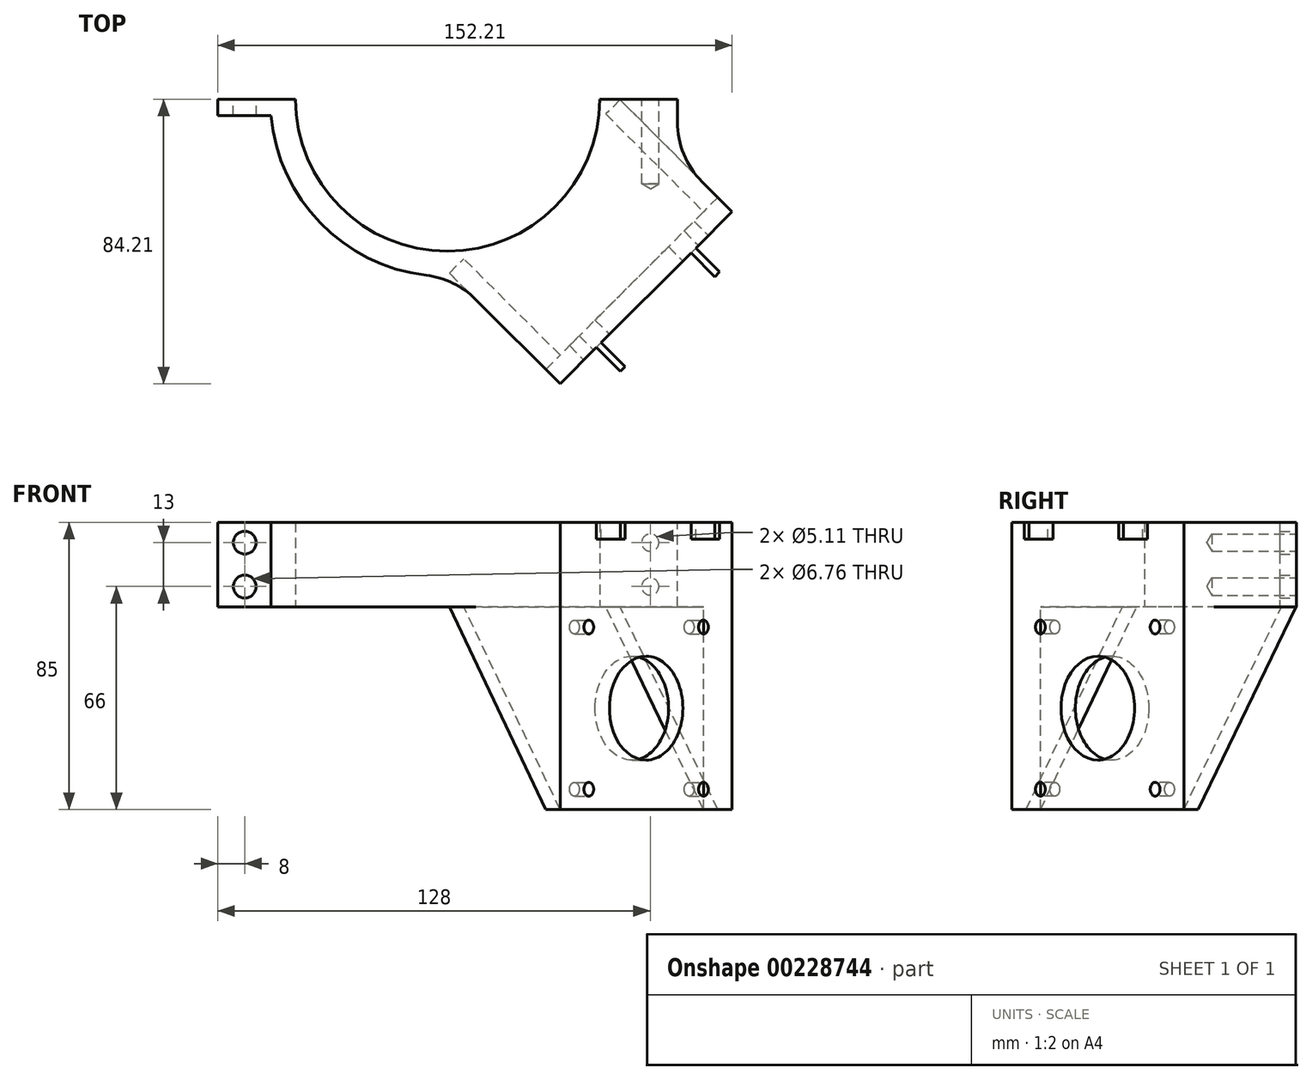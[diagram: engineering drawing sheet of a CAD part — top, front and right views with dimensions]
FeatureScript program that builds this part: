
annotation { "Feature Type Name" : "Feature", "Feature Type Description" : "" }
export const myFeature = defineFeature(function(context is Context, id is Id, definition is map)
    precondition{}
    {
        {
            var Q0;
            Q0=qCreatedBy(makeId("Top.planeOp"),FACE);
            var sketch = newSketch(context, id + "F0", { "sketchPlane" : qUnion([Q0])});
            skArc(sketch, "E0", {"start": v(-45, 0) * mm, "mid": v(0, -45) * mm, "end": v(45, 0) * mm});
            skArc(sketch, "E1", {"start": v(-52.27, -4.88) * mm, "mid": v(-31.78, -41.79) * mm, "end": v(9.25, -51.68) * mm});
            skLineSegment(sketch, "E2", {"start": v(-45, 0) * mm, "end": v(-68, 0) * mm});
            skLineSegment(sketch, "E3", {"start": v(-68, 0) * mm, "end": v(-68, -4.88) * mm});
            skLineSegment(sketch, "E4", {"start": v(-68, -4.88) * mm, "end": v(-52.27, -4.88) * mm});
            skLineSegment(sketch, "E5", {"start": v(45, 0) * mm, "end": v(68, 0) * mm});
            skLineSegment(sketch, "E6", {"start": v(68, 0) * mm, "end": v(68, -25.57) * mm});
            skPoint(sketch, "E7.orphan", {"position": v(52.5, 0) * mm});
            skLineSegment(sketch, "E8", {"start": v(0, 0) * mm, "end": v(69.96, -69.96) * mm, "construction": true});
            skLineSegment(sketch, "E9", {"start": v(68, -25.57) * mm, "end": v(79.96, -37.54) * mm});
            skLineSegment(sketch, "E10", {"start": v(79.96, -37.54) * mm, "end": v(37.54, -79.96) * mm});
            skLineSegment(sketch, "E11", {"start": v(37.54, -79.96) * mm, "end": v(9.25, -51.68) * mm});
            skPoint(sketch, "E12.orphan", {"position": v(68, -4.88) * mm});
            skSolve(sketch);
        }
        {
            var Q0;
            Q0 = qSketchRegion(id + "F0", true);
            extrude(context, id + "F1", {"entities" : qUnion([Q0]), "depth" : 25 * mm});
        }
        {
            var Q0;
            Q0=makeQuery(id+"F1.opExtrude","CAP_FACE",FACE,{"disambiguationData":[OSD([sQuery(id+"F0.wireOp",EDGE,"E0"),sQuery(id+"F0.wireOp",EDGE,"E1"),sQuery(id+"F0.wireOp",EDGE,"E2"),sQuery(id+"F0.wireOp",EDGE,"E3"),sQuery(id+"F0.wireOp",EDGE,"E4"),sQuery(id+"F0.wireOp",EDGE,"E5"),sQuery(id+"F0.wireOp",EDGE,"E6"),sQuery(id+"F0.wireOp",EDGE,"vUzMyOly-JOfE-7hCi-1u2C-14JDmTcw4MLE"),sQuery(id+"F0.wireOp",EDGE,"E9"),sQuery(id+"F0.wireOp",EDGE,"E10"),sQuery(id+"F0.wireOp",EDGE,"E11"),sQuery(id+"F0.wireOp",EDGE,"646cdaaa-5258-48e4-b4b1-44ca3091abd8.trimOffspring")])],"isStart":true});
            var sketch = newSketch(context, id + "F2", { "sketchPlane" : qUnion([Q0])});
            skLineSegment(sketch, "E13", {"start": v(37.54, 79.96) * mm, "end": v(79.96, 37.54) * mm});
            skLineSegment(sketch, "E14", {"start": v(79.96, 37.54) * mm, "end": v(75.72, 33.3) * mm});
            skLineSegment(sketch, "E15", {"start": v(75.72, 33.3) * mm, "end": v(33.3, 75.72) * mm});
            skLineSegment(sketch, "E16", {"start": v(33.3, 75.72) * mm, "end": v(37.54, 79.96) * mm});
            skSolve(sketch);
        }
        {
            var Q0;
            Q0 = qSketchRegion(id + "F2", true);
            extrude(context, id + "F3", {"entities" : qUnion([Q0]), "operationType" : NewBodyOperationType.ADD, "depth" : 60 * mm});
        }
        {
            var Q0;
            Q0=makeQuery(id+"F3.boolean.opBoolean","MERGE",FACE,{"derivedFrom":[makeQuery(id+"F1.opExtrude","SWEPT_FACE",FACE,{"disambiguationData":[OSD([sQuery(id+"F0.wireOp",EDGE,"E10")])]}),makeQuery(id+"F3.opExtrude","SWEPT_FACE",FACE,{"disambiguationData":[OSD([sQuery(id+"F2.wireOp",EDGE,"E13")])]})]});
            var sketch = newSketch(context, id + "F4", { "sketchPlane" : qUnion([Q0])});
            skCircle(sketch, "E17", {"center": v(0, -30) * mm, "radius": 15.37 * mm});
            skPoint(sketch, "E17.centerSnap0", {"position": v(0, -60) * mm});
            skLineSegment(sketch, "E18.direction1", {"start": v(-24, -54) * mm, "end": v(24, -54) * mm, "construction": true});
            skLineSegment(sketch, "E18.direction2", {"start": v(-24, -54) * mm, "end": v(-24, -6) * mm, "construction": true});
            skPoint(sketch, "E19", {"position": v(-24, -6) * mm});
            skPoint(sketch, "E20", {"position": v(-24, -54) * mm});
            skPoint(sketch, "E21", {"position": v(24, -54) * mm});
            skPoint(sketch, "E22", {"position": v(24, -6) * mm});
            skSolve(sketch);
        }
        {
            var Q0;
            Q0 = qSketchRegion(id + "F4", true);
            extrude(context, id + "F5", {"entities" : qUnion([Q0]), "operationType" : NewBodyOperationType.REMOVE, "endBound" : BoundingType.THROUGH_ALL, "oppositeDirection" : true, "depth" : 25 * mm});
        }
        {
            var Q0;
            Q0=makeQuery(id+"F1.opExtrude","CAP_FACE",FACE,{"disambiguationData":[OSD([sQuery(id+"F0.wireOp",EDGE,"E0"),sQuery(id+"F0.wireOp",EDGE,"E1"),sQuery(id+"F0.wireOp",EDGE,"E2"),sQuery(id+"F0.wireOp",EDGE,"E3"),sQuery(id+"F0.wireOp",EDGE,"E4"),sQuery(id+"F0.wireOp",EDGE,"E5"),sQuery(id+"F0.wireOp",EDGE,"E6"),sQuery(id+"F0.wireOp",EDGE,"vUzMyOly-JOfE-7hCi-1u2C-14JDmTcw4MLE"),sQuery(id+"F0.wireOp",EDGE,"E9"),sQuery(id+"F0.wireOp",EDGE,"E10"),sQuery(id+"F0.wireOp",EDGE,"E11"),sQuery(id+"F0.wireOp",EDGE,"646cdaaa-5258-48e4-b4b1-44ca3091abd8.trimOffspring")])],"isStart":false});
            var sketch = newSketch(context, id + "F6", { "sketchPlane" : qUnion([Q0])});
            skLineSegment(sketch, "E23", {"start": v(-68, 0) * mm, "end": v(79.96, 0) * mm, "construction": true});
            skSolve(sketch);
        }
        {
            var Q0;
            Q0=makeQuery(id+"F3.boolean.opBoolean","MERGE",FACE,{"derivedFrom":[makeQuery(id+"F1.opExtrude","SWEPT_FACE",FACE,{"disambiguationData":[OSD([sQuery(id+"F0.wireOp",EDGE,"E11")])]}),makeQuery(id+"F3.opExtrude","SWEPT_FACE",FACE,{"disambiguationData":[OSD([sQuery(id+"F2.wireOp",EDGE,"E16")])]})]});
            var sketch = newSketch(context, id + "F7", { "sketchPlane" : qUnion([Q0])});
            skLineSegment(sketch, "E24", {"start": v(83.08, 25) * mm, "end": v(83.08, -60) * mm});
            skLineSegment(sketch, "E25", {"start": v(83.08, -60) * mm, "end": v(77.08, -60) * mm});
            skLineSegment(sketch, "E26", {"start": v(77.08, -60) * mm, "end": v(36.79, 0) * mm});
            skLineSegment(sketch, "E27", {"start": v(36.79, 0) * mm, "end": v(36.79, 25) * mm});
            skLineSegment(sketch, "E28", {"start": v(36.79, 25) * mm, "end": v(83.08, 25) * mm});
            skSolve(sketch);
        }
        {
            var Q0;
            Q0 = qSketchRegion(id + "F7", true);
            extrude(context, id + "F8", {"entities" : qUnion([Q0]), "operationType" : NewBodyOperationType.ADD, "depth" : 6 * mm});
        }
        {
            var Q0;
            Q0=makeQuery(id+"F3.boolean.opBoolean","MERGE",FACE,{"derivedFrom":[makeQuery(id+"F1.opExtrude","SWEPT_FACE",FACE,{"disambiguationData":[OSD([sQuery(id+"F0.wireOp",EDGE,"E9")])]}),makeQuery(id+"F3.opExtrude","SWEPT_FACE",FACE,{"disambiguationData":[OSD([sQuery(id+"F2.wireOp",EDGE,"E14")])]})]});
            var sketch = newSketch(context, id + "F9", { "sketchPlane" : qUnion([Q0])});
            skLineSegment(sketch, "E29", {"start": v(-83.08, -60) * mm, "end": v(-83.08, 25) * mm});
            skLineSegment(sketch, "E30", {"start": v(-83.08, 25) * mm, "end": v(-36.18, 25) * mm});
            skLineSegment(sketch, "E31", {"start": v(-77.08, -60) * mm, "end": v(-83.08, -60) * mm});
            skLineSegment(sketch, "E32", {"start": v(-77.08, -60) * mm, "end": v(-36.18, 0) * mm});
            skLineSegment(sketch, "E33", {"start": v(-36.18, 0) * mm, "end": v(-36.18, 25) * mm});
            skSolve(sketch);
        }
        {
            var Q0;
            Q0 = qSketchRegion(id + "F9", true);
            extrude(context, id + "F10", {"entities" : qUnion([Q0]), "operationType" : NewBodyOperationType.ADD, "depth" : 6 * mm});
        }
        {
            var Q0;
            Q0=makeQuery(id+"F8.boolean.opBoolean","INTERSECT",EDGE,{"derivedFrom":[makeQuery(id+"F1.opExtrude","SWEPT_FACE",FACE,{"disambiguationData":[OSD([sQuery(id+"F0.wireOp",EDGE,"E1")])]}),makeQuery(id+"F8.opExtrude","CAP_FACE",FACE,{"disambiguationData":[OSD([sQuery(id+"F7.wireOp",EDGE,"E24"),sQuery(id+"F7.wireOp",EDGE,"E25"),sQuery(id+"F7.wireOp",EDGE,"E26"),sQuery(id+"F7.wireOp",EDGE,"E27"),sQuery(id+"F7.wireOp",EDGE,"E28")])],"isStart":false})]});
            fillet(context, id + "F11", {"entities" : qUnion([Q0]), "radius" : 25 * mm, "tangentPropagation" : true, "allowEdgeOverflow" : false});
        }
        {
            var Q0;
            Q0=makeQuery(id+"F10.boolean.opBoolean","INTERSECT",EDGE,{"derivedFrom":[makeQuery(id+"F1.opExtrude","SWEPT_FACE",FACE,{"disambiguationData":[OSD([sQuery(id+"F0.wireOp",EDGE,"E6")])]}),makeQuery(id+"F10.opExtrude","CAP_FACE",FACE,{"disambiguationData":[OSD([sQuery(id+"F9.wireOp",EDGE,"E29"),sQuery(id+"F9.wireOp",EDGE,"E30"),sQuery(id+"F9.wireOp",EDGE,"E31"),sQuery(id+"F9.wireOp",EDGE,"E32"),sQuery(id+"F9.wireOp",EDGE,"E33")])],"isStart":false})]});
            fillet(context, id + "F12", {"entities" : qUnion([Q0]), "radius" : 25 * mm, "tangentPropagation" : true, "allowEdgeOverflow" : false});
        }
        {
            var Q0;
            Q0=makeQuery(id+"F1.opExtrude","SWEPT_FACE",FACE,{"disambiguationData":[OSD([sQuery(id+"F0.wireOp",EDGE,"E2")])]});
            var sketch = newSketch(context, id + "F13", { "sketchPlane" : qUnion([Q0])});
            skLineSegment(sketch, "E34", {"start": v(60, -9.06) * mm, "end": v(60, 40.75) * mm, "construction": true});
            skLineSegment(sketch, "E35", {"start": v(-60, -8.44) * mm, "end": v(-60, 38.68) * mm, "construction": true});
            skPoint(sketch, "E36", {"position": v(60, 6) * mm});
            skPoint(sketch, "E37", {"position": v(60, 19) * mm});
            skPoint(sketch, "E38", {"position": v(-60, 6) * mm});
            skPoint(sketch, "E39", {"position": v(-60, 19) * mm});
            skSolve(sketch);
        }
        {
            var Q0;
            Q0=sQuery(id+"F13.wireOp",VERTEX,"E38");
            var Q1;
            Q1=sQuery(id+"F13.wireOp",VERTEX,"E39");
            var Q2;
            Q2=makeQuery(id+"F1.opExtrude","SWEPT_BODY",BODY,{"disambiguationData":[OSD([sQuery(id+"F0.wireOp",EDGE,"E0"),sQuery(id+"F0.wireOp",EDGE,"E1"),sQuery(id+"F0.wireOp",EDGE,"E2"),sQuery(id+"F0.wireOp",EDGE,"E3"),sQuery(id+"F0.wireOp",EDGE,"E4"),sQuery(id+"F0.wireOp",EDGE,"E5"),sQuery(id+"F0.wireOp",EDGE,"E6"),sQuery(id+"F0.wireOp",EDGE,"E9"),sQuery(id+"F0.wireOp",EDGE,"E10"),sQuery(id+"F0.wireOp",EDGE,"E11")])]});
            hole(context, id + "F14", {"style" : HoleStyle.SIMPLE, "endStyle" : HoleEndStyle.BLIND, "standardTappedOrClearance" : lookupTablePath({ "standard" : "ANSI", "engagement" : "75%", "pitch" : "20 tpi", "size" : "1/4", "type" : "Tapped" }), "standardBlindInLast" : lookupTablePath({ "standard" : "ANSI", "engagement" : "75%", "pitch" : "20 tpi", "size" : "1/4", "type" : "Tapped" }), "holeDiameter" : 5.1 * mm, "holeDepth" : 25 * mm, "locations" : qUnion([Q0, Q1]), "scope" : qUnion([Q2]), "majorDiameter" : 6.35 * mm});
        }
        {
            var Q0;
            Q0=sQuery(id+"F13.wireOp",VERTEX,"E36");
            var Q1;
            Q1=sQuery(id+"F13.wireOp",VERTEX,"E37");
            var Q2;
            Q2=makeQuery(id+"F1.opExtrude","SWEPT_BODY",BODY,{"disambiguationData":[OSD([sQuery(id+"F0.wireOp",EDGE,"E0"),sQuery(id+"F0.wireOp",EDGE,"E1"),sQuery(id+"F0.wireOp",EDGE,"E2"),sQuery(id+"F0.wireOp",EDGE,"E3"),sQuery(id+"F0.wireOp",EDGE,"E4"),sQuery(id+"F0.wireOp",EDGE,"E5"),sQuery(id+"F0.wireOp",EDGE,"E6"),sQuery(id+"F0.wireOp",EDGE,"E9"),sQuery(id+"F0.wireOp",EDGE,"E10"),sQuery(id+"F0.wireOp",EDGE,"E11")])]});
            hole(context, id + "F15", {"style" : HoleStyle.SIMPLE, "endStyle" : HoleEndStyle.BLIND, "standardTappedOrClearance" : lookupTablePath({ "standard" : "ANSI", "fit" : "Normal (ASME)", "size" : "1/4", "type" : "Clearance" }), "standardBlindInLast" : lookupTablePath({ "fit" : "Free", "standard" : "ANSI", "size" : "1/4", "type" : "Clearance" }), "holeDiameter" : 6.76 * mm, "holeDepth" : 25 * mm, "locations" : qUnion([Q0, Q1]), "scope" : qUnion([Q2])});
        }
        {
            var Q0;
            Q0=sQuery(id+"F4.wireOp",VERTEX,"E19");
            var Q1;
            Q1=sQuery(id+"F4.wireOp",VERTEX,"E22");
            var Q2;
            Q2=sQuery(id+"F4.wireOp",VERTEX,"E21");
            var Q3;
            Q3=sQuery(id+"F4.wireOp",VERTEX,"E20");
            var Q4;
            Q4=makeQuery(id+"F1.opExtrude","SWEPT_BODY",BODY,{"disambiguationData":[OSD([sQuery(id+"F0.wireOp",EDGE,"E0"),sQuery(id+"F0.wireOp",EDGE,"E1"),sQuery(id+"F0.wireOp",EDGE,"E2"),sQuery(id+"F0.wireOp",EDGE,"E3"),sQuery(id+"F0.wireOp",EDGE,"E4"),sQuery(id+"F0.wireOp",EDGE,"E5"),sQuery(id+"F0.wireOp",EDGE,"E6"),sQuery(id+"F0.wireOp",EDGE,"E9"),sQuery(id+"F0.wireOp",EDGE,"E10"),sQuery(id+"F0.wireOp",EDGE,"E11")])]});
            hole(context, id + "F16", {"style" : HoleStyle.SIMPLE, "endStyle" : HoleEndStyle.BLIND, "standardTappedOrClearance" : lookupTablePath({ "standard" : "ISO", "engagement" : "75%", "pitch" : "0.9 mm", "size" : "M5", "type" : "Tapped" }), "standardBlindInLast" : lookupTablePath({ "standard" : "ISO", "engagement" : "75%", "pitch" : "0.9 mm", "size" : "M5", "type" : "Tapped" }), "holeDiameter" : 4.1 * mm, "holeDepth" : 25 * mm, "locations" : qUnion([Q0, Q1, Q2, Q3]), "scope" : qUnion([Q4])});
        }
        {
            var Q0;
            Q0=makeQuery(id+"F6.imprint","IMPRINT",FACE,{"disambiguationData":[TD([[makeQuery(id+"F6.imprint","IMPRINT",EDGE,{"derivedFrom":makeQuery(id+"F1.opExtrude","CAP_EDGE",EDGE,{"disambiguationData":[OSD([sQuery(id+"F0.wireOp",EDGE,"E0")])],"isStart":false})}),-1.0]])]});
            var sketch = newSketch(context, id + "F17", { "sketchPlane" : qUnion([Q0])});
            skLineSegment(sketch, "E40", {"start": v(79.11, -52.53) * mm, "end": v(72.04, -45.46) * mm});
            skLineSegment(sketch, "E41", {"start": v(80.53, -51.11) * mm, "end": v(79.11, -52.53) * mm});
            skLineSegment(sketch, "E42", {"start": v(80.53, -51.11) * mm, "end": v(73.46, -44.04) * mm});
            skLineSegment(sketch, "E43", {"start": v(73.46, -44.04) * mm, "end": v(72.04, -45.46) * mm});
            skLineSegment(sketch, "E44", {"start": v(58.75, -58.75) * mm, "end": v(79.7, -79.7) * mm, "construction": true});
            skLineSegment(sketch, "E45.MirrorCS", {"start": v(52.53, -79.11) * mm, "end": v(45.46, -72.04) * mm});
            skLineSegment(sketch, "E46.MirrorCS", {"start": v(51.11, -80.53) * mm, "end": v(44.04, -73.46) * mm});
            skLineSegment(sketch, "E47.MirrorCS", {"start": v(51.11, -80.53) * mm, "end": v(52.53, -79.11) * mm});
            skLineSegment(sketch, "E48.MirrorCS", {"start": v(44.04, -73.46) * mm, "end": v(45.46, -72.04) * mm});
            skSolve(sketch);
        }
        {
            var Q0;
            Q0 = qSketchRegion(id + "F17", true);
            extrude(context, id + "F18", {"entities" : qUnion([Q0]), "operationType" : NewBodyOperationType.ADD, "oppositeDirection" : true, "depth" : 5 * mm});
        }
    });
